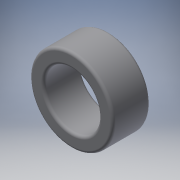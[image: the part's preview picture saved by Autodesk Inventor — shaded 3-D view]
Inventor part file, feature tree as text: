
AUTODESK INVENTOR PART (.ipt)
format: ipt  version: 2016 (Build 200138000, 138)  size: 141,824 bytes
history: native  units: mm
features: fillet x2, extrude x1, sketch x1
ambient origin geometry x8: Origin, YZ Plane, XZ Plane, XY Plane, X Axis, Y Axis, Z Axis, Center Point
bodies: Solid1 (feature_tree)
feature tree (4):
  extrude  "Extrusion1"  Depth=3.0mm
  fillet  "Fillet1"  Radius=40.0mm
  fillet  "Fillet2"  Radius=3.0mm
  sketch  "Sketch1"  dims[d0=58.5mm d1=15.0mm d2=40.0mm d3=0.0mm d4=3.0mm d5=3.0mm]
